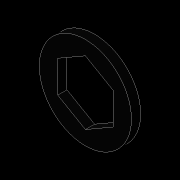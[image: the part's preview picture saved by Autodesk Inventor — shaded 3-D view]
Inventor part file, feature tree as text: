
AUTODESK INVENTOR PART (.ipt)
format: ipt  version: 2016 (Build 200138000, 138)  size: 80,896 bytes
history: native  units: in
note: dims shown in document units (in); Inventor stores cm internally (conversion verified against a paired STEP export)
features: extrude x1, sketch x1
ambient origin geometry x8: Origin, YZ Plane, XZ Plane, XY Plane, X Axis, Y Axis, Z Axis, Center Point
bodies: Solid1 (feature_tree)
feature tree (2):
  extrude  "Extrusion1"  Depth=0.0625in
  sketch  "Sketch1"  dims[d0=0.375in d1=0.625in d2=0.0625in d3=0.0in]
